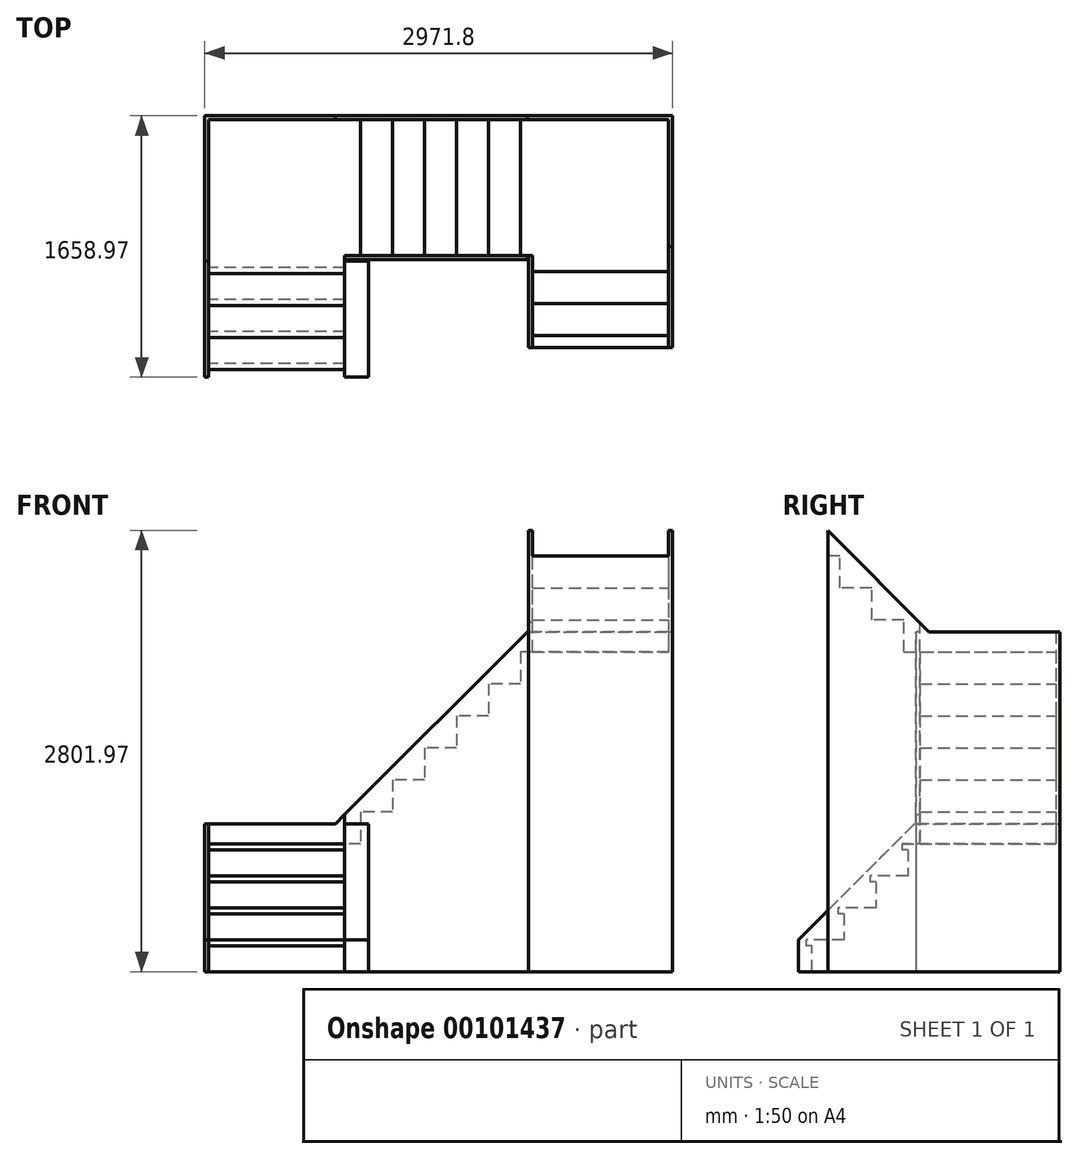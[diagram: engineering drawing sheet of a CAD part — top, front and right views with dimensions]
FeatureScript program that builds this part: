
annotation { "Feature Type Name" : "Feature", "Feature Type Description" : "" }
export const myFeature = defineFeature(function(context is Context, id is Id, definition is map)
    precondition{}
    {
        {
            var Q0;
            Q0=qCreatedBy(makeId("Right.planeOp"),FACE);
            var sketch = newSketch(context, id + "F0", { "sketchPlane" : qUnion([Q0])});
            skLineSegment(sketch, "E0", {"start": v(0, 0) * mm, "end": v(-1574.8, 0) * mm});
            skLineSegment(sketch, "E1", {"start": v(-1574.8, 0) * mm, "end": v(-1574.8, 203.2) * mm});
            skLineSegment(sketch, "E2", {"start": v(-1574.8, 203.2) * mm, "end": v(-1371.6, 203.2) * mm});
            skLineSegment(sketch, "E3", {"start": v(-1371.6, 203.2) * mm, "end": v(-1371.6, 406.4) * mm});
            skLineSegment(sketch, "E4", {"start": v(-1371.6, 406.4) * mm, "end": v(-1168.4, 406.4) * mm});
            skLineSegment(sketch, "E5", {"start": v(-1168.4, 406.4) * mm, "end": v(-1168.4, 609.6) * mm});
            skLineSegment(sketch, "E6", {"start": v(-1168.4, 609.6) * mm, "end": v(-965.2, 609.6) * mm});
            skLineSegment(sketch, "E7", {"start": v(-965.2, 609.6) * mm, "end": v(-965.2, 812.8) * mm});
            skLineSegment(sketch, "E8", {"start": v(-965.2, 812.8) * mm, "end": v(0, 812.8) * mm});
            skLineSegment(sketch, "E9", {"start": v(0, 812.8) * mm, "end": v(0, 0) * mm});
            skSolve(sketch);
        }
        {
            var Q0;
            Q0 = qSketchRegion(id + "F0", true);
            extrude(context, id + "F1", {"entities" : qUnion([Q0]), "depth" : 914.4 * mm});
        }
        {
            var Q0;
            Q0=makeQuery(id+"F1.opExtrude","SWEPT_FACE",FACE,{"disambiguationData":[OSD([sQuery(id+"F0.wireOp",EDGE,"E9")])]});
            var sketch = newSketch(context, id + "F2", { "sketchPlane" : qUnion([Q0])});
            skLineSegment(sketch, "E10", {"start": v(-914.4, 812.8) * mm, "end": v(-990.6, 812.8) * mm});
            skLineSegment(sketch, "E11", {"start": v(-990.6, 812.8) * mm, "end": v(-990.6, 1016) * mm});
            skLineSegment(sketch, "E12", {"start": v(-990.6, 1016) * mm, "end": v(-1193.8, 1016) * mm});
            skLineSegment(sketch, "E13", {"start": v(-1193.8, 1016) * mm, "end": v(-1193.8, 1219.2) * mm});
            skLineSegment(sketch, "E14", {"start": v(-1193.8, 1219.2) * mm, "end": v(-1397, 1219.2) * mm});
            skLineSegment(sketch, "E15", {"start": v(-1397, 1219.2) * mm, "end": v(-1397, 1422.4) * mm});
            skLineSegment(sketch, "E16", {"start": v(-1397, 1422.4) * mm, "end": v(-1600.2, 1422.4) * mm});
            skLineSegment(sketch, "E17", {"start": v(-1600.2, 1422.4) * mm, "end": v(-1600.2, 1625.6) * mm});
            skLineSegment(sketch, "E18", {"start": v(-1600.2, 1625.6) * mm, "end": v(-1803.4, 1625.6) * mm});
            skLineSegment(sketch, "E19", {"start": v(-1803.4, 1625.6) * mm, "end": v(-1803.4, 1828.8) * mm});
            skLineSegment(sketch, "E20", {"start": v(-1803.4, 1828.8) * mm, "end": v(-2006.6, 1828.8) * mm});
            skLineSegment(sketch, "E21", {"start": v(-2006.6, 1828.8) * mm, "end": v(-2006.6, 2032) * mm});
            skLineSegment(sketch, "E22", {"start": v(-2006.6, 2032) * mm, "end": v(-2971.8, 2032) * mm});
            skLineSegment(sketch, "E23", {"start": v(-2971.8, 2032) * mm, "end": v(-2971.8, 0) * mm});
            skLineSegment(sketch, "E24", {"start": v(-2971.8, 0) * mm, "end": v(-914.4, 0) * mm});
            skLineSegment(sketch, "E25", {"start": v(-914.4, 0) * mm, "end": v(-914.4, 812.8) * mm});
            skSolve(sketch);
        }
        {
            var Q0;
            Q0=makeQuery(id+"F2.imprint","IMPRINT",FACE,{"disambiguationData":[TD([[makeQuery(id+"F2.imprint","IMPRINT",EDGE,{"derivedFrom":sQuery(id+"F2.wireOp",EDGE,"E10")}),1.0]])]});
            extrude(context, id + "F3", {"entities" : qUnion([Q0]), "operationType" : NewBodyOperationType.ADD, "oppositeDirection" : true, "depth" : 914.4 * mm});
        }
        {
            var Q0;
            Q0=makeQuery(id+"F3.opExtrude","SWEPT_FACE",FACE,{"disambiguationData":[OSD([sQuery(id+"F2.wireOp",EDGE,"E23")])]});
            var sketch = newSketch(context, id + "F4", { "sketchPlane" : qUnion([Q0])});
            skLineSegment(sketch, "E26", {"start": v(-914.4, 2032) * mm, "end": v(-990.6, 2032) * mm});
            skLineSegment(sketch, "E27", {"start": v(-990.6, 2032) * mm, "end": v(-990.6, 2235.2) * mm});
            skLineSegment(sketch, "E28", {"start": v(-990.6, 2235.2) * mm, "end": v(-1193.8, 2235.2) * mm});
            skLineSegment(sketch, "E29", {"start": v(-1193.8, 2235.2) * mm, "end": v(-1193.8, 2438.4) * mm});
            skLineSegment(sketch, "E30", {"start": v(-1193.8, 2438.4) * mm, "end": v(-1397, 2438.4) * mm});
            skLineSegment(sketch, "E31", {"start": v(-1397, 2438.4) * mm, "end": v(-1397, 2641.6) * mm});
            skLineSegment(sketch, "E32", {"start": v(-1397, 2641.6) * mm, "end": v(-1473.2, 2641.6) * mm});
            skLineSegment(sketch, "E33", {"start": v(-1473.2, 2641.6) * mm, "end": v(-1473.2, 0) * mm});
            skLineSegment(sketch, "E34", {"start": v(-1473.2, 0) * mm, "end": v(-914.4, 0) * mm});
            skLineSegment(sketch, "E35", {"start": v(-914.4, 0) * mm, "end": v(-914.4, 2032) * mm});
            skSolve(sketch);
        }
        {
            var Q0;
            Q0 = qSketchRegion(id + "F4", true);
            extrude(context, id + "F5", {"entities" : qUnion([Q0]), "operationType" : NewBodyOperationType.ADD, "oppositeDirection" : true, "depth" : 914.4 * mm});
        }
        {
            var Q0;
            Q0=makeQuery(id+"F5.boolean.opBoolean","MERGE",FACE,{"derivedFrom":[makeQuery(id+"F3.opExtrude","SWEPT_FACE",FACE,{"disambiguationData":[OSD([sQuery(id+"F2.wireOp",EDGE,"E23")])]}),makeQuery(id+"F5.opExtrude","CAP_FACE",FACE,{"disambiguationData":[OSD([sQuery(id+"F4.wireOp",EDGE,"E26"),sQuery(id+"F4.wireOp",EDGE,"E27"),sQuery(id+"F4.wireOp",EDGE,"E28"),sQuery(id+"F4.wireOp",EDGE,"E29"),sQuery(id+"F4.wireOp",EDGE,"E30"),sQuery(id+"F4.wireOp",EDGE,"E31"),sQuery(id+"F4.wireOp",EDGE,"E32"),sQuery(id+"F4.wireOp",EDGE,"E33"),sQuery(id+"F4.wireOp",EDGE,"E34"),sQuery(id+"F4.wireOp",EDGE,"E35")])],"isStart":true})]});
            var sketch = newSketch(context, id + "F6", { "sketchPlane" : qUnion([Q0])});
            skLineSegment(sketch, "E36", {"start": v(-1473.2, 2514.6) * mm, "end": v(-1473.2, 2801.97) * mm});
            skLineSegment(sketch, "E37", {"start": v(-1473.2, 2801.97) * mm, "end": v(-830.23, 2159) * mm});
            skLineSegment(sketch, "E38", {"start": v(-830.23, 2159) * mm, "end": v(0, 2159) * mm});
            skLineSegment(sketch, "E39", {"start": v(0, 2159) * mm, "end": v(0, 2032) * mm});
            skLineSegment(sketch, "E40", {"start": v(0, 2032) * mm, "end": v(-990.6, 2032) * mm});
            skLineSegment(sketch, "E41", {"start": v(-990.6, 2032) * mm, "end": v(-1473.2, 2514.6) * mm});
            skSolve(sketch);
        }
        {
            var Q0;
            Q0 = qSketchRegion(id + "F6", true);
            extrude(context, id + "F7", {"entities" : qUnion([Q0]), "operationType" : NewBodyOperationType.ADD, "oppositeDirection" : true, "depth" : 25.4 * mm});
        }
        {
            var Q0;
            Q0=makeQuery(id+"F7.boolean.opBoolean","MERGE",FACE,{"derivedFrom":[makeQuery(id+"F3.boolean.opBoolean","MERGE",FACE,{"derivedFrom":[makeQuery(id+"F1.opExtrude","SWEPT_FACE",FACE,{"disambiguationData":[OSD([sQuery(id+"F0.wireOp",EDGE,"E9")])]}),makeQuery(id+"F3.opExtrude","CAP_FACE",FACE,{"disambiguationData":[OSD([sQuery(id+"F2.wireOp",EDGE,"E10"),sQuery(id+"F2.wireOp",EDGE,"E11"),sQuery(id+"F2.wireOp",EDGE,"E12"),sQuery(id+"F2.wireOp",EDGE,"E13"),sQuery(id+"F2.wireOp",EDGE,"E14"),sQuery(id+"F2.wireOp",EDGE,"E15"),sQuery(id+"F2.wireOp",EDGE,"E16"),sQuery(id+"F2.wireOp",EDGE,"E17"),sQuery(id+"F2.wireOp",EDGE,"E18"),sQuery(id+"F2.wireOp",EDGE,"E19"),sQuery(id+"F2.wireOp",EDGE,"E20"),sQuery(id+"F2.wireOp",EDGE,"E21"),sQuery(id+"F2.wireOp",EDGE,"E22"),sQuery(id+"F2.wireOp",EDGE,"E23"),sQuery(id+"F2.wireOp",EDGE,"E24"),sQuery(id+"F2.wireOp",EDGE,"E25")])],"isStart":true})]}),makeQuery(id+"F7.opExtrude","SWEPT_FACE",FACE,{"disambiguationData":[OSD([sQuery(id+"F6.wireOp",EDGE,"E39")])]})]});
            var sketch = newSketch(context, id + "F8", { "sketchPlane" : qUnion([Q0])});
            skLineSegment(sketch, "E42", {"start": v(-2946.4, 2159) * mm, "end": v(-2049.43, 2159) * mm});
            skLineSegment(sketch, "E43", {"start": v(-2049.43, 2159) * mm, "end": v(-830.23, 939.8) * mm});
            skLineSegment(sketch, "E44", {"start": v(-830.23, 939.8) * mm, "end": v(0, 939.8) * mm});
            skLineSegment(sketch, "E45", {"start": v(0, 939.8) * mm, "end": v(0, 812.8) * mm});
            skLineSegment(sketch, "E46", {"start": v(0, 812.8) * mm, "end": v(-990.6, 812.8) * mm});
            skLineSegment(sketch, "E47", {"start": v(-990.6, 812.8) * mm, "end": v(-2209.8, 2032) * mm});
            skLineSegment(sketch, "E48", {"start": v(-2209.8, 2032) * mm, "end": v(-2946.4, 2032) * mm});
            skLineSegment(sketch, "E49", {"start": v(-2946.4, 2032) * mm, "end": v(-2946.4, 2159) * mm});
            skSolve(sketch);
        }
        {
            var Q0;
            Q0 = qSketchRegion(id + "F8", true);
            extrude(context, id + "F9", {"entities" : qUnion([Q0]), "operationType" : NewBodyOperationType.ADD, "oppositeDirection" : true, "depth" : 25.4 * mm});
        }
        {
            var Q0;
            Q0=makeQuery(id+"F9.boolean.opBoolean","MERGE",FACE,{"derivedFrom":[makeQuery(id+"F1.opExtrude","CAP_FACE",FACE,{"disambiguationData":[OSD([sQuery(id+"F0.wireOp",EDGE,"E0"),sQuery(id+"F0.wireOp",EDGE,"E1"),sQuery(id+"F0.wireOp",EDGE,"E2"),sQuery(id+"F0.wireOp",EDGE,"E3"),sQuery(id+"F0.wireOp",EDGE,"E4"),sQuery(id+"F0.wireOp",EDGE,"E5"),sQuery(id+"F0.wireOp",EDGE,"E6"),sQuery(id+"F0.wireOp",EDGE,"E7"),sQuery(id+"F0.wireOp",EDGE,"E8"),sQuery(id+"F0.wireOp",EDGE,"E9")])],"isStart":true}),makeQuery(id+"F9.opExtrude","SWEPT_FACE",FACE,{"disambiguationData":[OSD([sQuery(id+"F8.wireOp",EDGE,"E45")])]})]});
            var sketch = newSketch(context, id + "F10", { "sketchPlane" : qUnion([Q0])});
            skLineSegment(sketch, "E50", {"start": v(25.4, 939.8) * mm, "end": v(922.37, 939.8) * mm});
            skLineSegment(sketch, "E51", {"start": v(922.37, 939.8) * mm, "end": v(1658.97, 203.2) * mm});
            skLineSegment(sketch, "E52", {"start": v(1658.97, 203.2) * mm, "end": v(1658.97, 0) * mm});
            skLineSegment(sketch, "E53", {"start": v(1658.97, 0) * mm, "end": v(1574.8, 0) * mm});
            skLineSegment(sketch, "E54", {"start": v(1574.8, 0) * mm, "end": v(762, 812.8) * mm});
            skLineSegment(sketch, "E55", {"start": v(762, 812.8) * mm, "end": v(25.4, 812.8) * mm});
            skLineSegment(sketch, "E56", {"start": v(25.4, 812.8) * mm, "end": v(25.4, 939.8) * mm});
            skSolve(sketch);
        }
        {
            var Q0;
            Q0 = qSketchRegion(id + "F10", true);
            extrude(context, id + "F11", {"entities" : qUnion([Q0]), "operationType" : NewBodyOperationType.ADD, "oppositeDirection" : true, "depth" : 25.4 * mm});
        }
        {
            var Q0;
            Q0=makeQuery(id+"F5.opExtrude","CAP_FACE",FACE,{"disambiguationData":[OSD([sQuery(id+"F4.wireOp",EDGE,"E26"),sQuery(id+"F4.wireOp",EDGE,"E27"),sQuery(id+"F4.wireOp",EDGE,"E28"),sQuery(id+"F4.wireOp",EDGE,"E29"),sQuery(id+"F4.wireOp",EDGE,"E30"),sQuery(id+"F4.wireOp",EDGE,"E31"),sQuery(id+"F4.wireOp",EDGE,"E32"),sQuery(id+"F4.wireOp",EDGE,"E33"),sQuery(id+"F4.wireOp",EDGE,"E34"),sQuery(id+"F4.wireOp",EDGE,"E35")])],"isStart":false});
            var sketch = newSketch(context, id + "F12", { "sketchPlane" : qUnion([Q0])});
            skLineSegment(sketch, "E57", {"start": v(889, 2217.77) * mm, "end": v(1473.2, 2801.97) * mm});
            skLineSegment(sketch, "E58", {"start": v(1473.2, 2801.97) * mm, "end": v(1473.2, 2641.6) * mm});
            skLineSegment(sketch, "E59", {"start": v(1473.2, 2514.6) * mm, "end": v(990.6, 2032) * mm});
            skLineSegment(sketch, "E60", {"start": v(990.6, 2032) * mm, "end": v(889, 2032) * mm});
            skLineSegment(sketch, "E61", {"start": v(889, 2032) * mm, "end": v(889, 2217.77) * mm});
            skLineSegment(sketch, "E62", {"start": v(1473.2, 2641.6) * mm, "end": v(1473.2, 2514.6) * mm});
            skSolve(sketch);
        }
        {
            var Q0;
            Q0 = qSketchRegion(id + "F12", true);
            extrude(context, id + "F13", {"entities" : qUnion([Q0]), "operationType" : NewBodyOperationType.ADD, "oppositeDirection" : true, "depth" : 25.4 * mm});
        }
        {
            var Q0;
            Q0=makeQuery(id+"F13.opExtrude","SWEPT_FACE",FACE,{"disambiguationData":[OSD([sQuery(id+"F12.wireOp",EDGE,"E61")])]});
            var sketch = newSketch(context, id + "F14", { "sketchPlane" : qUnion([Q0])});
            skLineSegment(sketch, "E63", {"start": v(-889, 998.57) * mm, "end": v(-2049.43, 2159) * mm});
            skLineSegment(sketch, "E64", {"start": v(-2049.43, 2159) * mm, "end": v(-2082.8, 2159) * mm});
            skLineSegment(sketch, "E65", {"start": v(-2082.8, 2159) * mm, "end": v(-2082.8, 1905) * mm});
            skLineSegment(sketch, "E66", {"start": v(-2082.8, 1905) * mm, "end": v(-990.6, 812.8) * mm});
            skLineSegment(sketch, "E67", {"start": v(-990.6, 812.8) * mm, "end": v(-889, 812.8) * mm});
            skLineSegment(sketch, "E68", {"start": v(-889, 812.8) * mm, "end": v(-889, 998.57) * mm});
            skSolve(sketch);
        }
        {
            var Q0;
            Q0 = qSketchRegion(id + "F14", true);
            extrude(context, id + "F15", {"entities" : qUnion([Q0]), "operationType" : NewBodyOperationType.ADD, "oppositeDirection" : true, "depth" : 25.4 * mm});
        }
        {
            var Q0;
            Q0=makeQuery(id+"F15.boolean.opBoolean","MERGE",FACE,{"derivedFrom":[makeQuery(id+"F3.opExtrude","CAP_FACE",FACE,{"disambiguationData":[OSD([sQuery(id+"F2.wireOp",EDGE,"E10"),sQuery(id+"F2.wireOp",EDGE,"E11"),sQuery(id+"F2.wireOp",EDGE,"E12"),sQuery(id+"F2.wireOp",EDGE,"E13"),sQuery(id+"F2.wireOp",EDGE,"E14"),sQuery(id+"F2.wireOp",EDGE,"E15"),sQuery(id+"F2.wireOp",EDGE,"E16"),sQuery(id+"F2.wireOp",EDGE,"E17"),sQuery(id+"F2.wireOp",EDGE,"E18"),sQuery(id+"F2.wireOp",EDGE,"E19"),sQuery(id+"F2.wireOp",EDGE,"E20"),sQuery(id+"F2.wireOp",EDGE,"E21"),sQuery(id+"F2.wireOp",EDGE,"E22"),sQuery(id+"F2.wireOp",EDGE,"E23"),sQuery(id+"F2.wireOp",EDGE,"E24"),sQuery(id+"F2.wireOp",EDGE,"E25")])],"isStart":false}),makeQuery(id+"F15.opExtrude","CAP_FACE",FACE,{"disambiguationData":[OSD([sQuery(id+"F14.wireOp",EDGE,"E63"),sQuery(id+"F14.wireOp",EDGE,"E64"),sQuery(id+"F14.wireOp",EDGE,"E65"),sQuery(id+"F14.wireOp",EDGE,"E66"),sQuery(id+"F14.wireOp",EDGE,"E67"),sQuery(id+"F14.wireOp",EDGE,"E68")])],"isStart":false})]});
            var sketch = newSketch(context, id + "F16", { "sketchPlane" : qUnion([Q0])});
            skLineSegment(sketch, "E69.bottom", {"start": v(914.4, 0) * mm, "end": v(2057.4, 0) * mm});
            skLineSegment(sketch, "E69.top", {"start": v(914.4, 2641.6) * mm, "end": v(2057.4, 2641.6) * mm});
            skLineSegment(sketch, "E69.left", {"start": v(914.4, 0) * mm, "end": v(914.4, 2641.6) * mm});
            skLineSegment(sketch, "E69.right", {"start": v(2057.4, 0) * mm, "end": v(2057.4, 2641.6) * mm});
            skSolve(sketch);
        }
        {
            var Q0;
            Q0=makeQuery(id+"F1.opExtrude","CAP_FACE",FACE,{"disambiguationData":[OSD([sQuery(id+"F0.wireOp",EDGE,"E0"),sQuery(id+"F0.wireOp",EDGE,"E1"),sQuery(id+"F0.wireOp",EDGE,"E2"),sQuery(id+"F0.wireOp",EDGE,"E3"),sQuery(id+"F0.wireOp",EDGE,"E4"),sQuery(id+"F0.wireOp",EDGE,"E5"),sQuery(id+"F0.wireOp",EDGE,"E6"),sQuery(id+"F0.wireOp",EDGE,"E7"),sQuery(id+"F0.wireOp",EDGE,"E8"),sQuery(id+"F0.wireOp",EDGE,"E9")])],"isStart":false});
            var sketch = newSketch(context, id + "F17", { "sketchPlane" : qUnion([Q0])});
            skLineSegment(sketch, "E70.0.0", {"start": v(-1574.8, 0) * mm, "end": v(-914.4, 0) * mm});
            skLineSegment(sketch, "E70.0.1", {"start": v(-914.4, 0) * mm, "end": v(-914.4, 609.6) * mm});
            skLineSegment(sketch, "E70.0.2", {"start": v(-914.4, 609.6) * mm, "end": v(-1168.4, 609.6) * mm});
            skLineSegment(sketch, "E70.0.3", {"start": v(-1168.4, 609.6) * mm, "end": v(-1168.4, 406.4) * mm});
            skLineSegment(sketch, "E70.0.4", {"start": v(-1168.4, 406.4) * mm, "end": v(-1371.6, 406.4) * mm});
            skLineSegment(sketch, "E70.0.5", {"start": v(-1371.6, 406.4) * mm, "end": v(-1371.6, 203.2) * mm});
            skLineSegment(sketch, "E70.0.6", {"start": v(-1371.6, 203.2) * mm, "end": v(-1574.8, 203.2) * mm});
            skLineSegment(sketch, "E70.0.7", {"start": v(-1574.8, 203.2) * mm, "end": v(-1574.8, 0) * mm});
            skSolve(sketch);
        }
        {
            var Q0;
            Q0=makeQuery(id+"FYT3tzW4MferEoW_1.boolean.opBoolean","MERGE",FACE,{"derivedFrom":[makeQuery(id+"F1.opExtrude","SWEPT_FACE",FACE,{"disambiguationData":[OSD([sQuery(id+"F0.wireOp",EDGE,"E3")])]}),makeQuery(id+"FYT3tzW4MferEoW_1.opExtrude","SWEPT_FACE",FACE,{"disambiguationData":[OSD([sQuery(id+"F17.wireOp",EDGE,"E70.0.5")])]})]});
            var sketch = newSketch(context, id + "F18", { "sketchPlane" : qUnion([Q0])});
            skLineSegment(sketch, "E71", {"start": v(1828.8, 203.2) * mm, "end": v(1625.6, 203.2) * mm});
            skLineSegment(sketch, "E72", {"start": v(1625.6, 203.2) * mm, "end": v(1625.6, 406.4) * mm});
            skLineSegment(sketch, "E73", {"start": v(1625.6, 406.4) * mm, "end": v(1422.4, 406.4) * mm});
            skLineSegment(sketch, "E74", {"start": v(1422.4, 406.4) * mm, "end": v(1422.4, 609.6) * mm});
            skLineSegment(sketch, "E75", {"start": v(1422.4, 609.6) * mm, "end": v(1828.8, 609.6) * mm});
            skLineSegment(sketch, "E76", {"start": v(1828.8, 609.6) * mm, "end": v(1828.8, 203.2) * mm});
            skSolve(sketch);
        }
        {
            var Q0;
            Q0 = qSketchRegion(id + "F18", true);
            var Q1;
            Q1=makeQuery(id+"F15.boolean.opBoolean","MERGE",FACE,{"derivedFrom":[makeQuery(id+"F3.opExtrude","CAP_FACE",FACE,{"disambiguationData":[OSD([sQuery(id+"F2.wireOp",EDGE,"E10"),sQuery(id+"F2.wireOp",EDGE,"E11"),sQuery(id+"F2.wireOp",EDGE,"E12"),sQuery(id+"F2.wireOp",EDGE,"E13"),sQuery(id+"F2.wireOp",EDGE,"E14"),sQuery(id+"F2.wireOp",EDGE,"E15"),sQuery(id+"F2.wireOp",EDGE,"E16"),sQuery(id+"F2.wireOp",EDGE,"E17"),sQuery(id+"F2.wireOp",EDGE,"E18"),sQuery(id+"F2.wireOp",EDGE,"E19"),sQuery(id+"F2.wireOp",EDGE,"E20"),sQuery(id+"F2.wireOp",EDGE,"E21"),sQuery(id+"F2.wireOp",EDGE,"E22"),sQuery(id+"F2.wireOp",EDGE,"E23"),sQuery(id+"F2.wireOp",EDGE,"E24"),sQuery(id+"F2.wireOp",EDGE,"E25")])],"isStart":false}),makeQuery(id+"F15.opExtrude","CAP_FACE",FACE,{"disambiguationData":[OSD([sQuery(id+"F14.wireOp",EDGE,"E63"),sQuery(id+"F14.wireOp",EDGE,"E64"),sQuery(id+"F14.wireOp",EDGE,"E65"),sQuery(id+"F14.wireOp",EDGE,"E66"),sQuery(id+"F14.wireOp",EDGE,"E67"),sQuery(id+"F14.wireOp",EDGE,"E68")])],"isStart":false})]});
            extrude(context, id + "F19", {"entities" : qUnion([Q0]), "operationType" : NewBodyOperationType.REMOVE, "endBound" : BoundingType.UP_TO_SURFACE, "oppositeDirection" : true, "endBoundEntityFace" : qUnion([Q1]), "depth" : 25.4 * mm});
        }
        {
            var Q0;
            Q0=makeQuery(id+"F1.opExtrude","CAP_FACE",FACE,{"disambiguationData":[OSD([sQuery(id+"F0.wireOp",EDGE,"E0"),sQuery(id+"F0.wireOp",EDGE,"E1"),sQuery(id+"F0.wireOp",EDGE,"E2"),sQuery(id+"F0.wireOp",EDGE,"E3"),sQuery(id+"F0.wireOp",EDGE,"E4"),sQuery(id+"F0.wireOp",EDGE,"E5"),sQuery(id+"F0.wireOp",EDGE,"E6"),sQuery(id+"F0.wireOp",EDGE,"E7"),sQuery(id+"F0.wireOp",EDGE,"E8"),sQuery(id+"F0.wireOp",EDGE,"E9")])],"isStart":false});
            var sketch = newSketch(context, id + "F20", { "sketchPlane" : qUnion([Q0])});
            skLineSegment(sketch, "E77", {"start": v(-1658.97, 0) * mm, "end": v(-1658.97, 203.2) * mm});
            skLineSegment(sketch, "E78", {"start": v(-1658.97, 203.2) * mm, "end": v(-922.37, 939.8) * mm});
            skLineSegment(sketch, "E79", {"start": v(-922.37, 939.8) * mm, "end": v(-889, 939.8) * mm});
            skLineSegment(sketch, "E80", {"start": v(-889, 939.8) * mm, "end": v(-889, 0) * mm});
            skLineSegment(sketch, "E81", {"start": v(-889, 0) * mm, "end": v(-1658.97, 0) * mm});
            skSolve(sketch);
        }
        {
            var Q0;
            Q0 = qSketchRegion(id + "F20", true);
            extrude(context, id + "F21", {"entities" : qUnion([Q0]), "operationType" : NewBodyOperationType.ADD, "oppositeDirection" : true, "depth" : 25.4 * mm, "hasSecondDirection" : true, "secondDirectionOppositeDirection" : false, "secondDirectionDepth" : 127 * mm});
        }
        {
            var Q0;
            Q0=makeQuery(id+"F11.boolean.opBoolean","MERGE",FACE,{"derivedFrom":[makeQuery(id+"F9.boolean.opBoolean","MERGE",FACE,{"derivedFrom":[makeQuery(id+"F1.opExtrude","CAP_FACE",FACE,{"disambiguationData":[OSD([sQuery(id+"F0.wireOp",EDGE,"E0"),sQuery(id+"F0.wireOp",EDGE,"E1"),sQuery(id+"F0.wireOp",EDGE,"E2"),sQuery(id+"F0.wireOp",EDGE,"E3"),sQuery(id+"F0.wireOp",EDGE,"E4"),sQuery(id+"F0.wireOp",EDGE,"E5"),sQuery(id+"F0.wireOp",EDGE,"E6"),sQuery(id+"F0.wireOp",EDGE,"E7"),sQuery(id+"F0.wireOp",EDGE,"E8"),sQuery(id+"F0.wireOp",EDGE,"E9")])],"isStart":true}),makeQuery(id+"F9.opExtrude","SWEPT_FACE",FACE,{"disambiguationData":[OSD([sQuery(id+"F8.wireOp",EDGE,"E45")])]})]}),makeQuery(id+"F11.opExtrude","CAP_FACE",FACE,{"disambiguationData":[OSD([sQuery(id+"F10.wireOp",EDGE,"E50"),sQuery(id+"F10.wireOp",EDGE,"E51"),sQuery(id+"F10.wireOp",EDGE,"E52"),sQuery(id+"F10.wireOp",EDGE,"E53"),sQuery(id+"F10.wireOp",EDGE,"E54"),sQuery(id+"F10.wireOp",EDGE,"E55"),sQuery(id+"F10.wireOp",EDGE,"E56")])],"isStart":true})]});
            var sketch = newSketch(context, id + "F22", { "sketchPlane" : qUnion([Q0])});
            skLineSegment(sketch, "E82.bottom", {"start": v(965.2, 812.8) * mm, "end": v(1003.3, 812.8) * mm});
            skLineSegment(sketch, "E82.top", {"start": v(965.2, 774.7) * mm, "end": v(1003.3, 774.7) * mm});
            skLineSegment(sketch, "E82.left", {"start": v(965.2, 812.8) * mm, "end": v(965.2, 774.7) * mm});
            skLineSegment(sketch, "E82.right", {"start": v(1003.3, 812.8) * mm, "end": v(1003.3, 774.7) * mm});
            skLineSegment(sketch, "E83.bottom", {"start": v(1168.4, 609.6) * mm, "end": v(1206.5, 609.6) * mm});
            skLineSegment(sketch, "E83.top", {"start": v(1168.4, 571.5) * mm, "end": v(1206.5, 571.5) * mm});
            skLineSegment(sketch, "E83.left", {"start": v(1168.4, 609.6) * mm, "end": v(1168.4, 571.5) * mm});
            skLineSegment(sketch, "E83.right", {"start": v(1206.5, 609.6) * mm, "end": v(1206.5, 571.5) * mm});
            skLineSegment(sketch, "E84.bottom", {"start": v(1371.6, 406.4) * mm, "end": v(1409.7, 406.4) * mm});
            skLineSegment(sketch, "E84.top", {"start": v(1371.6, 368.3) * mm, "end": v(1409.7, 368.3) * mm});
            skLineSegment(sketch, "E84.left", {"start": v(1371.6, 406.4) * mm, "end": v(1371.6, 368.3) * mm});
            skLineSegment(sketch, "E84.right", {"start": v(1409.7, 406.4) * mm, "end": v(1409.7, 368.3) * mm});
            skLineSegment(sketch, "E85.bottom", {"start": v(1574.8, 203.2) * mm, "end": v(1612.9, 203.2) * mm});
            skLineSegment(sketch, "E85.top", {"start": v(1574.8, 165.1) * mm, "end": v(1612.9, 165.1) * mm});
            skLineSegment(sketch, "E85.left", {"start": v(1574.8, 203.2) * mm, "end": v(1574.8, 165.1) * mm});
            skLineSegment(sketch, "E85.right", {"start": v(1612.9, 203.2) * mm, "end": v(1612.9, 165.1) * mm});
            skSolve(sketch);
        }
        {
            var Q0;
            Q0 = qSketchRegion(id + "F22", true);
            var Q1;
            Q1=makeQuery(id+"F21.boolean.opBoolean","MERGE",FACE,{"derivedFrom":[makeQuery(id+"F15.opExtrude","SWEPT_FACE",FACE,{"disambiguationData":[OSD([sQuery(id+"F14.wireOp",EDGE,"E68")])]}),makeQuery(id+"F21.opExtrude","CAP_FACE",FACE,{"disambiguationData":[OSD([sQuery(id+"F20.wireOp",EDGE,"E77"),sQuery(id+"F20.wireOp",EDGE,"E78"),sQuery(id+"F20.wireOp",EDGE,"E79"),sQuery(id+"F20.wireOp",EDGE,"E80"),sQuery(id+"F20.wireOp",EDGE,"E81")])],"isStart":false})]});
            extrude(context, id + "F23", {"entities" : qUnion([Q0]), "operationType" : NewBodyOperationType.ADD, "endBound" : BoundingType.UP_TO_SURFACE, "oppositeDirection" : true, "endBoundEntityFace" : qUnion([Q1]), "depth" : 25.4 * mm});
        }
    });
